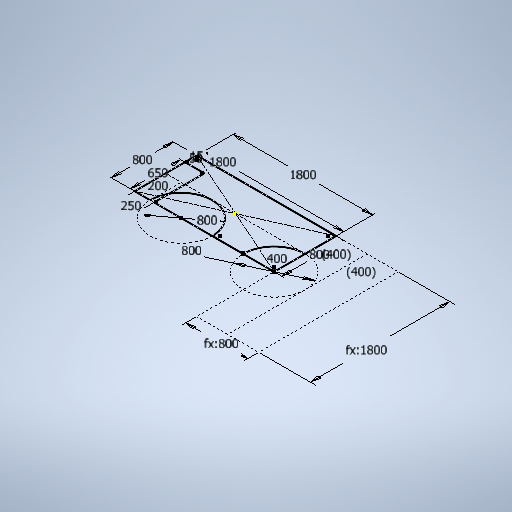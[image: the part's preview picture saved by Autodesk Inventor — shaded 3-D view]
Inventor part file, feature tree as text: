
AUTODESK INVENTOR PART (.ipt)
format: ipt  version: 2025.2 (Build 292293000, 293)  size: 292,864 bytes
history: native  units: mm
features: sketch x2
ambient origin geometry x8: Origin, YZ Plane, XZ Plane, XY Plane, X Axis, Y Axis, Z Axis, Center Point
feature tree (2):
  sketch  "Esboço1"  dims[d0=800.0mm]
  sketch  "Esboço3"  dims[d1=1800.0mm d3=650.0mm d5=15.0mm d6=800.0mm d7=1800.0mm d9=250.0mm d11=800.0mm d13=400.0mm d14=400.0mm d15=400.0mm d16=1800.0mm d17=800.0mm d19=200.0mm d20=50.0mm d21=800.0mm d22=0.5mm d23=0.872665mm d24=0.5mm d25=0.872665mm]
